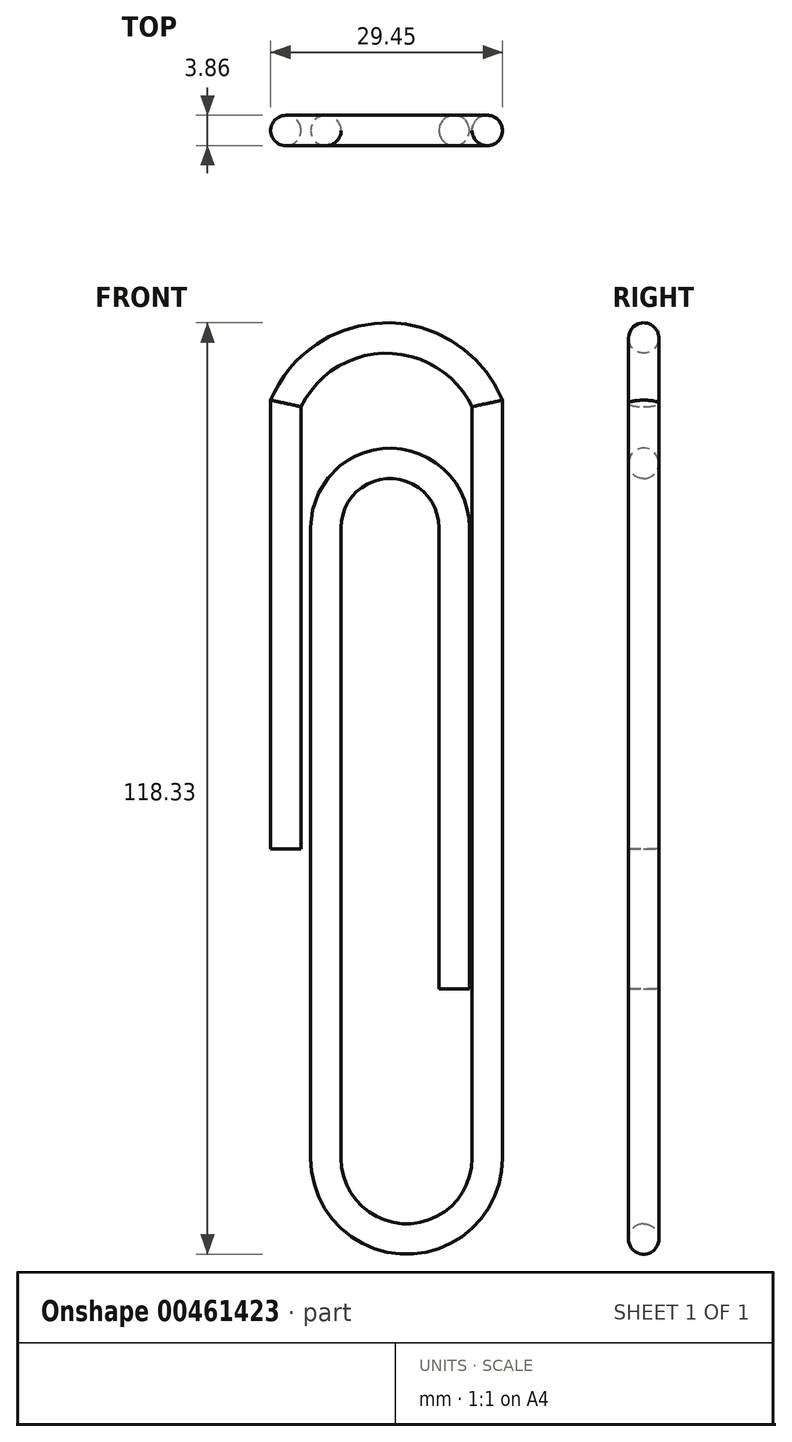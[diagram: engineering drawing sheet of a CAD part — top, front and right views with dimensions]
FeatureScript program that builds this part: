
annotation { "Feature Type Name" : "Feature", "Feature Type Description" : "" }
export const myFeature = defineFeature(function(context is Context, id is Id, definition is map)
    precondition{}
    {
        {
            var Q0;
            Q0=qCreatedBy(makeId("Front.planeOp"),FACE);
            var sketch = newSketch(context, id + "F0", { "sketchPlane" : qUnion([Q0])});
            skLineSegment(sketch, "E0", {"start": v(0, 0) * mm, "end": v(0, 56.62) * mm});
            skArc(sketch, "E1", {"start": v(25.59, 56.62) * mm, "mid": v(12.8, 64.94) * mm, "end": v(0, 56.62) * mm});
            skLineSegment(sketch, "E2", {"start": v(25.59, 56.62) * mm, "end": v(25.59, -39.28) * mm});
            skArc(sketch, "E3", {"start": v(5.1, -39.28) * mm, "mid": v(15.34, -49.53) * mm, "end": v(25.59, -39.28) * mm});
            skLineSegment(sketch, "E4", {"start": v(5.1, -39.28) * mm, "end": v(5.1, 40.86) * mm});
            skArc(sketch, "E5", {"start": v(21.38, 40.86) * mm, "mid": v(13.24, 49) * mm, "end": v(5.1, 40.86) * mm});
            skLineSegment(sketch, "E6", {"start": v(21.38, 40.86) * mm, "end": v(21.38, -17.74) * mm});
            skSolve(sketch);
        }
        {
            var Q0;
            Q0=qCreatedBy(makeId("Top.planeOp"),FACE);
            var sketch = newSketch(context, id + "F1", { "sketchPlane" : qUnion([Q0])});
            skCircle(sketch, "E7", {"center": v(0, 0) * mm, "radius": 1.93 * mm});
            skSolve(sketch);
        }
        {
            var Q0;
            Q0=makeQuery(id+"F1.imprint","IMPRINT",FACE,{"disambiguationData":[TD([[makeQuery(id+"F1.imprint","IMPRINT",EDGE,{"derivedFrom":sQuery(id+"F1.wireOp",EDGE,"E7")}),1.0]])]});
            var Q1;
            Q1=sQuery(id+"F0.wireOp",EDGE,"E0");
            var Q2;
            Q2=sQuery(id+"F0.wireOp",EDGE,"E1");
            var Q3;
            Q3=sQuery(id+"F0.wireOp",EDGE,"E2");
            var Q4;
            Q4=sQuery(id+"F0.wireOp",EDGE,"E4");
            var Q5;
            Q5=sQuery(id+"F0.wireOp",EDGE,"E3");
            var Q6;
            Q6=sQuery(id+"F0.wireOp",EDGE,"E6");
            var Q7;
            Q7=sQuery(id+"F0.wireOp",EDGE,"E5");
            sweep(context, id + "F2", {"profiles" : qUnion([Q0]), "path" : qUnion([Q1, Q2, Q3, Q4, Q5, Q6, Q7])});
        }
    });
